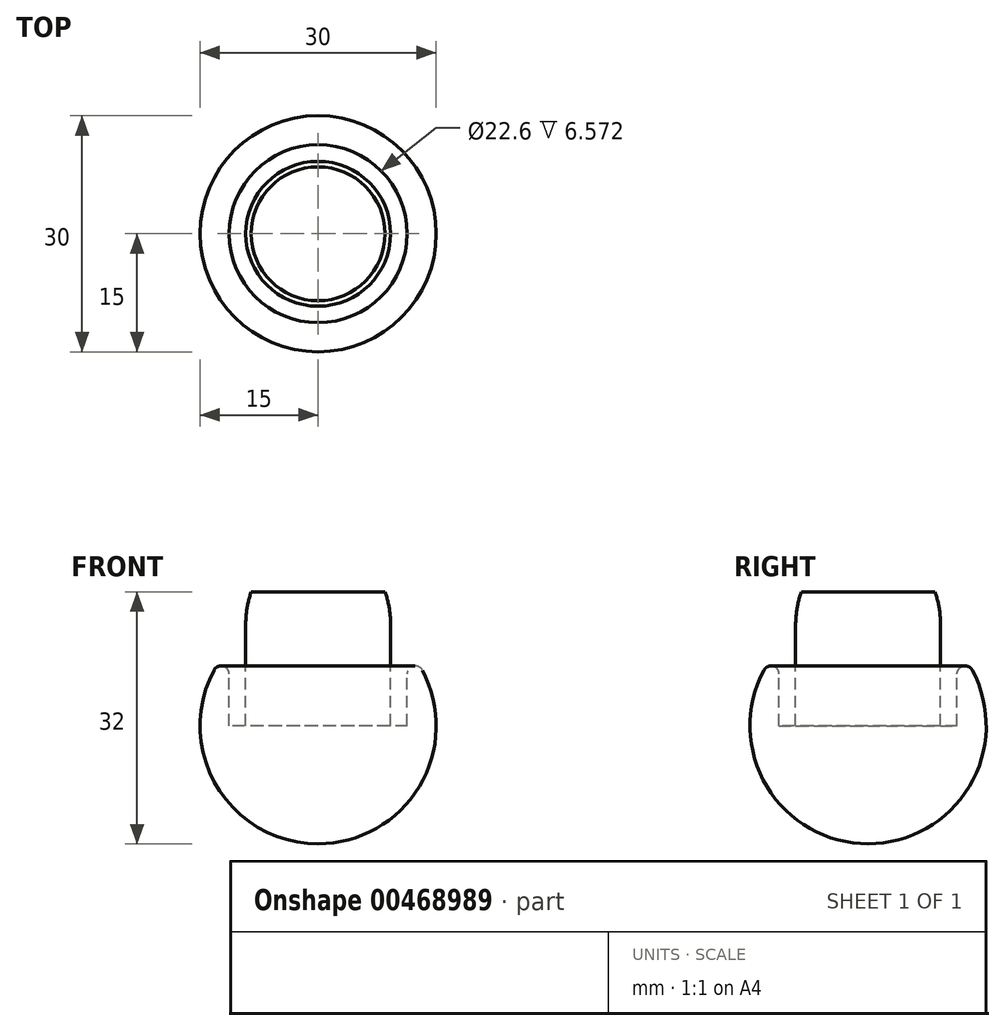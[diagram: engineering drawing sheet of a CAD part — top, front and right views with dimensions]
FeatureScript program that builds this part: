
annotation { "Feature Type Name" : "Feature", "Feature Type Description" : "" }
export const myFeature = defineFeature(function(context is Context, id is Id, definition is map)
    precondition{}
    {
        {
            var Q0;
            Q0=qCreatedBy(makeId("Front.planeOp"),FACE);
            var sketch = newSketch(context, id + "F0", { "sketchPlane" : qUnion([Q0])});
            skLineSegment(sketch, "E0", {"start": v(0, 37.35) * mm, "end": v(0, -41.4) * mm, "construction": true});
            skLineSegment(sketch, "E1", {"start": v(0, 17) * mm, "end": v(8.5, 17) * mm});
            skLineSegment(sketch, "E2", {"start": v(9.2, 12.88) * mm, "end": v(9.2, 0) * mm});
            skLineSegment(sketch, "E3", {"start": v(9.2, 0) * mm, "end": v(11.3, 0) * mm});
            skLineSegment(sketch, "E4", {"start": v(11.3, 0) * mm, "end": v(11.3, 0) * mm});
            skArc(sketch, "E5", {"start": v(0, -15) * mm, "mid": v(12.86, -7.72) * mm, "end": v(13.24, 7.06) * mm});
            skLineSegment(sketch, "E6", {"start": v(11.3, 0) * mm, "end": v(11.3, 6.57) * mm});
            skLineSegment(sketch, "E7", {"start": v(0, 17) * mm, "end": v(0, -15) * mm});
            skArc(sketch, "E8", {"start": v(13.24, 7.06) * mm, "mid": v(12.08, 7.57) * mm, "end": v(11.3, 6.57) * mm});
            skArc(sketch, "E9", {"start": v(9.2, 12.88) * mm, "mid": v(9.02, 14.97) * mm, "end": v(8.5, 17) * mm});
            skPoint(sketch, "E10.orphan", {"position": v(9.2, 15) * mm});
            skSolve(sketch);
        }
        {
            var Q0;
            Q0=makeQuery(id+"F0.imprint","IMPRINT",FACE,{"disambiguationData":[TD([[makeQuery(id+"F0.imprint","IMPRINT",EDGE,{"derivedFrom":sQuery(id+"F0.wireOp",EDGE,"E1")}),-1.0]])]});
            var Q1;
            Q1=sQuery(id+"F0.wireOp",EDGE,"E0");
            revolve(context, id + "F1", {"entities" : qUnion([Q0]), "axis" : qUnion([Q1]), "revolveType" : RevolveType.FULL});
        }
    });
